# Revit family: heroal D 72 Single Door - In - Continuous - Fanlight 1x Sidelight
name_source: partatom
category: Türen
revit_build: Autodesk Revit 2017 (Build: 20160225_1515(x64)
units: mm (PartAtom-declared; Revit-internal decimal feet)

## family parameters
Basisbauteil = Wand
Beim Laden mit Abzugskörper schneiden = Nein
Gemeinsam genutzt = Nein
Immer vertikal = Ja
OmniClass-Nummer = 23.30.10.00
OmniClass-Titel = Doors
Raumberechnungspunkt = Nein

## types (1)
- 1600x2700
    Ability To Bear Safety Equipment DIN EN 14351 = Fullfilled
    Air Permeability DIN EN 12207 = 4
    Analytische Konstruktion = <None>
    Baugruppenkennzeichen = B2030110
    Beschreibung = heroal D 72 Aluminium Door Systems
    Breite = 1600 mm  [stored 5.24934 ft]
    Burglary Resistance DIN V ENV 1627 = RC1-RC3
    Continuous Function DIN EN 12400 = 6/8
    Edition number = 1
    Glass = heroal Glass
    Heat Insulation [Uf in W/m2K] DIN EN ISO 10077 = 1,7
    Heat Insulation [Uf in W/m2K]/Standard Profile View DIN EN ISO 10077 = 1.7/145
    Heat Insulation [Uw in W/m2K] DIN EN ISO 10077-1 = 0,9
    Hersteller = heroal
    Höhe = 2700 mm  [stored 8.85827 ft]
    Max. Casement Leaf Height = 3000mm
    Max. Casement Weight = 180kg
    Max. Thickness Of Glass/Infill Panel = 66mm
    Mechanical Durability DIN EN 13115 = 3
    Modell = heroal D 72 60/33
    Operating forces DIN EN 12217 = 2
    Product Guid = 6ad9ed1e-4e62-4a3a-9421-3177d500a871
    Profile Installation Depth - Casement Profiles = 72/82
    Profile Installation Depth - Cross Bar Profiles = 72mm
    Profile Installation Depth - Frame Profiles = 72mm
    Profile View Width - Casement Profiles = 56-124mm
    Profile View Width - Cross Bar Profiles = 70-254mm
    Profile View Width - Frame Profiles = 60-250mm
    Reveal Left = 20 mm  [stored 0.0656168 ft]
    Reveal Right = 20 mm  [stored 0.0656168 ft]
    Reveal Top = 20 mm  [stored 0.0656168 ft]
    Rohbaubreite = 1600 mm  [stored 5.24934 ft]
    Rohbauhöhe = 2700 mm  [stored 8.85827 ft]
    Shock Resistance DIN EN 13049 = 4
    Soundproofing Class DIN EN ISO 717-1 = 1-3
    Tightness Against Driving Rain DIN EN 12208 = 9A
    URL = http://www.heroal.com
    Wandabschluss = Nach Basisbauteil
    Wind Load Resistance DIN EN 12210 = C4

note: [stored X ft] marks values corroborated as IEEE doubles in the binary element streams (Revit-internal decimal feet)

## geometry (parser evidence)
native form markers: Blend x6, Sweep x25
no freeform markers — native parametric forms only
